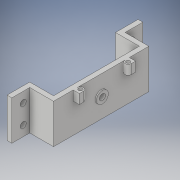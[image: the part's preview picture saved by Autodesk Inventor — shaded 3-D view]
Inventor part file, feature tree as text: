
AUTODESK INVENTOR PART (.ipt)
format: ipt  version: 2019 (Build 230136000, 136)  size: 214,016 bytes
history: native  units: mm
features: sketch x9, extrude x8, hole x2
ambient origin geometry x8: Origin, YZ Plane, XZ Plane, XY Plane, X Axis, Y Axis, Z Axis, Center Point
bodies: Solid1 (feature_tree)
feature tree (19):
  extrude  "Extrusion1"  Depth=19.0mm
  extrude  "Extrusion2"  Depth=19.0mm
  extrude  "Extrusion3"  Depth=5.0mm
  extrude  "Extrusion4"  Depth=24.0mm
  extrude  "Extrusion5"  Depth=24.0mm
  hole  "Hole1"  [1 undecoded]
  sketch  "Sketch7"  dims[d17=4.0mm d18=80.0mm]
  hole  "Hole2"  [1 undecoded]
  extrude  "Extrusion6"  Depth=33.0mm TaperAngle=0.0deg
  extrude  "Extrusion7"  Depth=4.0mm
  extrude  "Extrusion8"  Depth=24.0mm
  sketch  "Sketch1"  dims[d0=33.0mm d1=19.0mm]
  sketch  "Sketch2"  dims[d2=33.0mm d3=19.0mm]
  sketch  "Sketch3"  dims[d6=5.0mm d8=5.0mm]
  sketch  "Sketch4"  dims[d9=4.0mm d10=0.0mm d11=24.0mm]
  sketch  "Sketch5"  dims[d12=4.0mm d13=24.0mm]
  sketch  "Sketch6"  dims[d14=33.0mm d15=0.0mm d16=80.0mm]
  sketch  "Sketch8"  dims[d19=4.0mm d20=33.0mm d21=0.0mm]
  sketch  "Sketch9"  dims[d22=24.0mm d23=4.0mm d24=24.0mm d25=4.0mm d26=33.0mm d27=0.0mm d28=19.0mm d29=4.0mm d30=19.0mm d31=4.0mm d32=33.0mm d33=0.0mm d36=5.0mm d38=5.0mm d39=5.0mm d40=6.0mm d41=4.0mm d42=2.0mm d43=90.0deg d44=8.0mm d45=20.594885mm d46=10.0mm d47=5.0mm d48=5.0mm d49=6.0mm d50=4.0mm d51=2.0mm d52=90.0deg d53=8.0mm d54=20.594885mm d55=1.0mm d56=0.0mm d58=5.2mm d59=6.2mm d60=5.2mm d61=6.2mm d62=2.6mm d63=3.2mm d64=8.0mm d65=0.0mm d67=5.2mm d68=6.2mm d69=5.2mm d70=6.2mm d71=2.6mm d72=3.2mm d73=8.0mm d74=0.0mm d57=0.0625mm]
note: 2 required parameter values undecoded (feature->parameter linkage not recoverable at this tier; creation-order binding heuristic only, values carry confidence <= 0.55)
